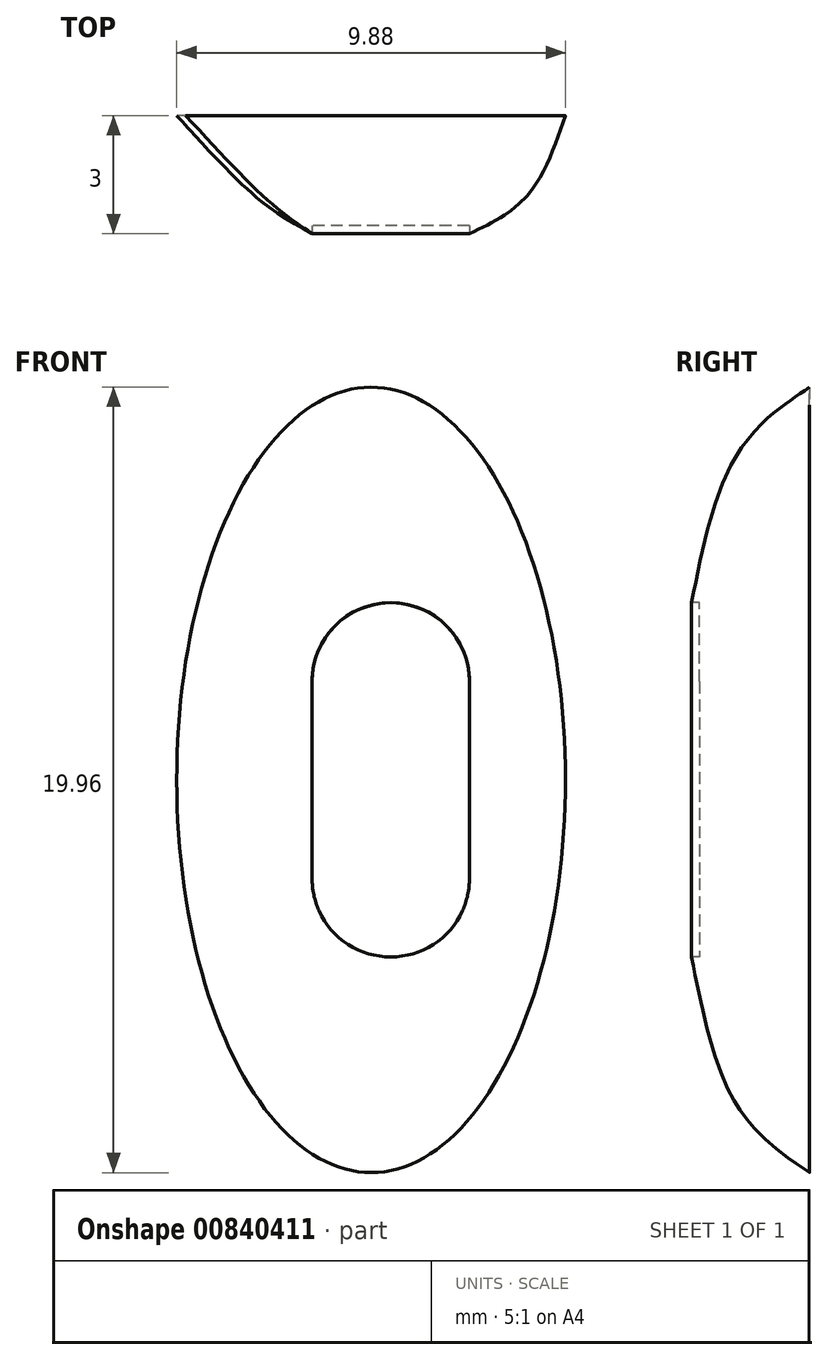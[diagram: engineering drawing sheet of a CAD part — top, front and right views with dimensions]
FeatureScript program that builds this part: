
annotation { "Feature Type Name" : "Feature", "Feature Type Description" : "" }
export const myFeature = defineFeature(function(context is Context, id is Id, definition is map)
    precondition{}
    {
        {
            var Q0;
            Q0=qCreatedBy(makeId("Front.planeOp"),FACE);
            var sketch = newSketch(context, id + "F0", { "sketchPlane" : qUnion([Q0])});
            skLineSegment(sketch, "E0", {"start": v(0, -2.5) * mm, "end": v(0, 2.5) * mm, "construction": true});
            skLineSegment(sketch, "E1", {"start": v(-2, 2.5) * mm, "end": v(-2, -2.5) * mm});
            skLineSegment(sketch, "E2", {"start": v(2, 2.5) * mm, "end": v(2, -2.5) * mm});
            skArc(sketch, "E3", {"start": v(-2, -2.5) * mm, "mid": v(-1.96, -2.92) * mm, "end": v(-1.82, -3.32) * mm});
            skArc(sketch, "E4", {"start": v(2, 2.5) * mm, "mid": v(1.95, 2.94) * mm, "end": v(1.8, 3.37) * mm});
            skLineSegment(sketch, "E5", {"start": v(2, 2.5) * mm, "end": v(-2, 2.5) * mm, "construction": true});
            skArc(sketch, "E6", {"start": v(-1.8, 3.37) * mm, "mid": v(-1.95, 2.94) * mm, "end": v(-2, 2.5) * mm});
            skArc(sketch, "E7", {"start": v(1.8, 3.37) * mm, "mid": v(0, 4.5) * mm, "end": v(-1.8, 3.37) * mm});
            skArc(sketch, "E8", {"start": v(-1.82, -3.32) * mm, "mid": v(0, -4.5) * mm, "end": v(1.82, -3.32) * mm});
            skArc(sketch, "E9", {"start": v(1.82, -3.32) * mm, "mid": v(1.96, -2.92) * mm, "end": v(2, -2.5) * mm});
            skSolve(sketch);
        }
        {
            var Q0;
            Q0=qCreatedBy(makeId("Front.planeOp"),FACE);
            cPlane(context, id + "F1", {"entities" : qUnion([Q0]), "cplaneType" : CPlaneType.OFFSET, "offset" : 1 * mm, "oppositeDirection" : true, "width" : 150 * mm, "height" : 150 * mm});
        }
        {
            var Q0;
            Q0=qCreatedBy(id+"F1.planeOp",FACE);
            var sketch = newSketch(context, id + "F2", { "sketchPlane" : qUnion([Q0])});
            skEllipse(sketch, "E10", {"center": v(0, 0) * mm, "majorRadius": 8 * mm, "minorRadius": 3.5 * mm, "majorAxis": v(0, 1)});
            skSolve(sketch);
        }
        {
            var Q0;
            Q0=qCreatedBy(id+"F1.planeOp",FACE);
            cPlane(context, id + "F3", {"entities" : qUnion([Q0]), "cplaneType" : CPlaneType.OFFSET, "offset" : 2 * mm, "oppositeDirection" : true, "width" : 150 * mm, "height" : 150 * mm});
        }
        {
            var Q0;
            Q0=qCreatedBy(id+"F3.planeOp",FACE);
            var sketch = newSketch(context, id + "F4", { "sketchPlane" : qUnion([Q0])});
            skEllipse(sketch, "E11", {"center": v(-0.5, 0) * mm, "majorRadius": 9.98 * mm, "minorRadius": 4.94 * mm, "majorAxis": v(0, 1)});
            skSolve(sketch);
        }
        {
            var Q0;
            Q0 = qSketchRegion(id + "F0", true);
            var Q1;
            Q1 = qSketchRegion(id + "F2", true);
            var Q2;
            Q2 = qSketchRegion(id + "F4", true);
            loft(context, id + "F5", {"sheetProfilesArray" : [{ "sheetProfileEntities" : qUnion([Q0]) }, { "sheetProfileEntities" : qUnion([Q1]) }, { "sheetProfileEntities" : qUnion([Q2]) }]});
        }
        {
            var Q0;
            Q0=makeQuery(id+"F0.imprint","IMPRINT",FACE,{"disambiguationData":[TD([[makeQuery(id+"F0.imprint","IMPRINT",EDGE,{"derivedFrom":sQuery(id+"F0.wireOp",EDGE,"E1")}),1.0]])]});
            extrude(context, id + "F6", {"entities" : qUnion([Q0]), "operationType" : NewBodyOperationType.REMOVE, "oppositeDirection" : true, "depth" : 0.2 * mm, "offsetDistance" : 25 * mm});
        }
    });
